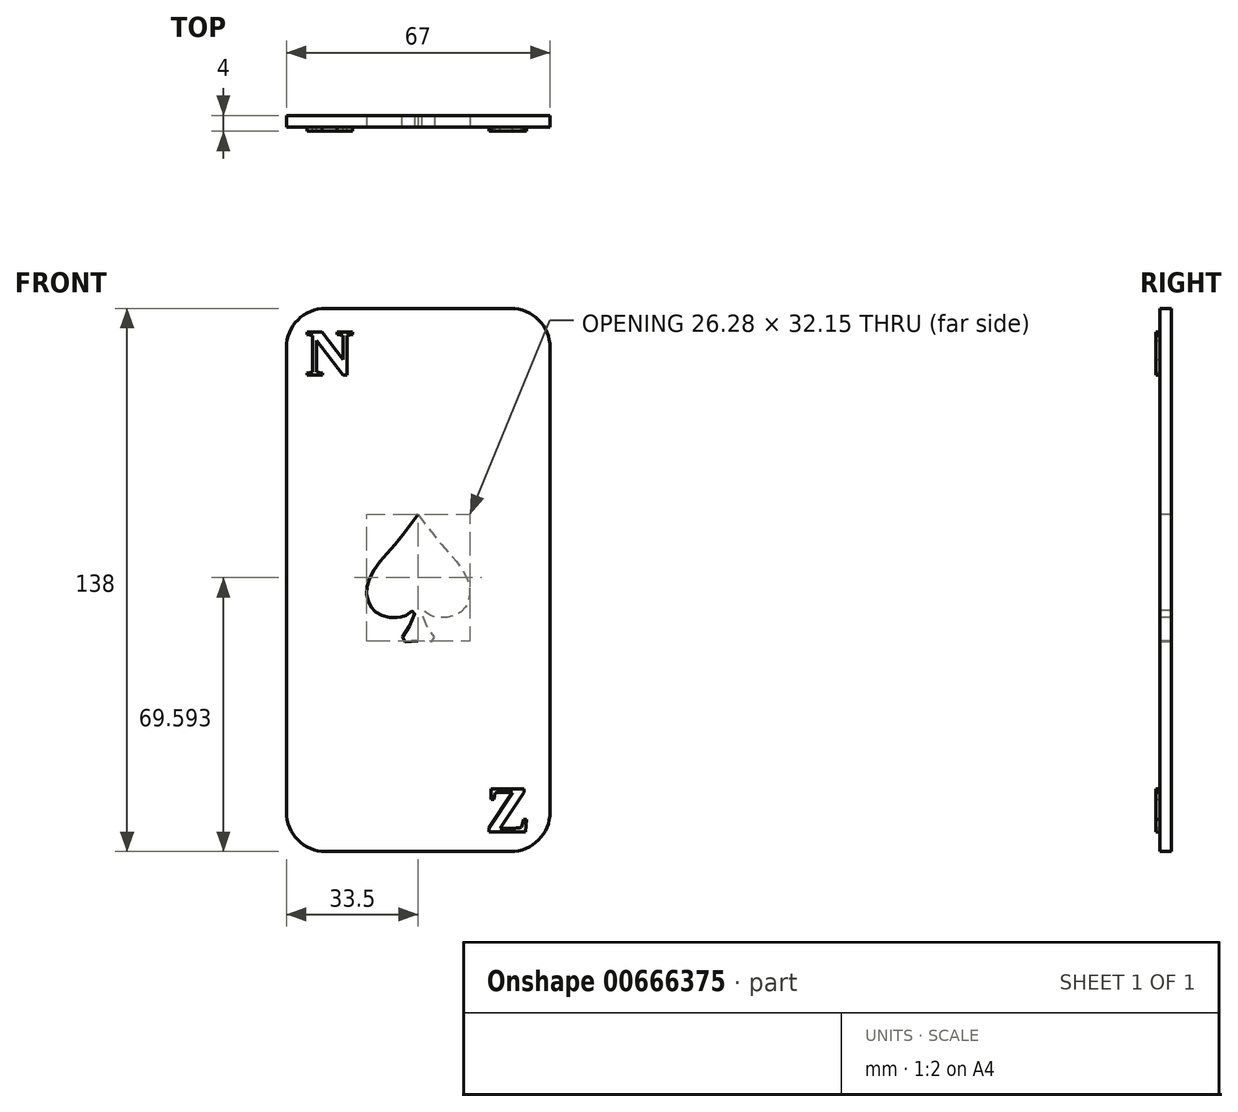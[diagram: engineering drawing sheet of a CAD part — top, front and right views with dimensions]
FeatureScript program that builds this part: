
annotation { "Feature Type Name" : "Feature", "Feature Type Description" : "" }
export const myFeature = defineFeature(function(context is Context, id is Id, definition is map)
    precondition{}
    {
        {
            var Q0;
            Q0=qCreatedBy(makeId("Front.planeOp"),FACE);
            var sketch = newSketch(context, id + "F0", { "sketchPlane" : qUnion([Q0])});
            skLineSegment(sketch, "E0.bottom", {"start": v(-23.5, 69) * mm, "end": v(23.5, 69) * mm});
            skLineSegment(sketch, "E0.top", {"start": v(-23.5, -69) * mm, "end": v(23.5, -69) * mm});
            skLineSegment(sketch, "E0.left", {"start": v(-33.5, 59) * mm, "end": v(-33.5, -59) * mm});
            skLineSegment(sketch, "E0.right", {"start": v(33.5, 59) * mm, "end": v(33.5, -59) * mm});
            skPoint(sketch, "E1.visualSharp", {"position": v(-33.5, 69) * mm});
            skArc(sketch, "E1.filletArc", {"start": v(-23.5, 69) * mm, "mid": v(-30.57, 66.07) * mm, "end": v(-33.5, 59) * mm});
            skPoint(sketch, "E2.visualSharp", {"position": v(33.5, 69) * mm});
            skArc(sketch, "E2.filletArc", {"start": v(33.5, 59) * mm, "mid": v(30.57, 66.07) * mm, "end": v(23.5, 69) * mm});
            skPoint(sketch, "E3.visualSharp", {"position": v(33.5, -69) * mm});
            skArc(sketch, "E3.filletArc", {"start": v(23.5, -69) * mm, "mid": v(30.57, -66.07) * mm, "end": v(33.5, -59) * mm});
            skPoint(sketch, "E4.visualSharp", {"position": v(-33.5, -69) * mm});
            skArc(sketch, "E4.filletArc", {"start": v(-33.5, -59) * mm, "mid": v(-30.57, -66.07) * mm, "end": v(-23.5, -69) * mm});
            skSolve(sketch);
        }
        {
            var Q0;
            Q0=makeQuery(id+"F0.imprint","IMPRINT",FACE,{"disambiguationData":[TD([[makeQuery(id+"F0.imprint","IMPRINT",EDGE,{"derivedFrom":sQuery(id+"F0.wireOp",EDGE,"E0.bottom")}),-1.0]])]});
            var sketch = newSketch(context, id + "F1", { "sketchPlane" : qUnion([Q0])});
            skText(sketch, "E5", { "text": "N", "fontName": "Tinos-Bold.ttf"});
            skText(sketch, "E6", { "text": "Z", "fontName": "Tinos-Bold.ttf"});
            const initialGuessF1  = {"E5": [-0.0285, 0.052, 1, 0, 0.012], "E6": [0.01719, -0.064, 1, 0, 0.012]};
            skSetInitialGuess(sketch, initialGuessF1);
            skSolve(sketch);
        }
        {
            var Q0;
            Q0=makeQuery(id+"F0.imprint","IMPRINT",FACE,{"disambiguationData":[TD([[makeQuery(id+"F0.imprint","IMPRINT",EDGE,{"derivedFrom":sQuery(id+"F0.wireOp",EDGE,"E0.bottom")}),-1.0]])]});
            var sketch = newSketch(context, id + "F2", { "sketchPlane" : qUnion([Q0])});
            skFitSpline(sketch, "E7", {"points": [v(0, 16.67) * mm, v(-3.59, 11.84) * mm, v(-7.27, 7.34) * mm, v(-10.17, 4.1) * mm, v(-12.13, 1) * mm, v(-13.02, -1.58) * mm, v(-13.06, -3.97) * mm, v(-12.55, -5.85) * mm, v(-11.95, -7.02) * mm, v(-10.8, -8.14) * mm, v(-8.93, -9.16) * mm, v(-6.8, -9.59) * mm, v(-5.13, -9.52) * mm, v(-4.55, -9.44) * mm, v(-3.77, -9.31) * mm, v(-2.5, -8.72) * mm, v(-1.05, -7.78) * mm, v(-1.64, -10.82) * mm, v(-4.15, -15.36) * mm, v(0, -15.48) * mm], "startDerivative": vector(-43.7, -59.68) * mm, "endDerivative": vector(87, 12.12) * mm});
            skFitSpline(sketch, "E8.MirrorCS", {"points": [v(0, 16.67) * mm, v(3.59, 11.84) * mm, v(7.27, 7.34) * mm, v(10.17, 4.1) * mm, v(12.13, 1) * mm, v(13.02, -1.58) * mm, v(13.06, -3.97) * mm, v(12.55, -5.85) * mm, v(11.95, -7.02) * mm, v(10.8, -8.14) * mm, v(8.93, -9.16) * mm, v(6.8, -9.59) * mm, v(5.13, -9.52) * mm, v(4.55, -9.44) * mm, v(3.77, -9.31) * mm, v(2.5, -8.72) * mm, v(1.05, -7.78) * mm, v(1.64, -10.82) * mm, v(4.15, -15.36) * mm, v(0, -15.48) * mm], "startDerivative": vector(43.7, -59.68) * mm, "endDerivative": vector(-87, 12.12) * mm});
            skSolve(sketch);
        }
        {
            var Q0;
            Q0=makeQuery(id+"F0.imprint","IMPRINT",FACE,{"disambiguationData":[TD([[makeQuery(id+"F0.imprint","IMPRINT",EDGE,{"derivedFrom":sQuery(id+"F0.wireOp",EDGE,"E0.bottom")}),-1.0]])]});
            extrude(context, id + "F3", {"entities" : qUnion([Q0]), "depth" : 3 * mm, "offsetDistance" : 25 * mm});
        }
        {
            var Q0;
            Q0=makeQuery(id+"F2.imprint","IMPRINT",FACE,{"disambiguationData":[TD([[makeQuery(id+"F2.imprint","IMPRINT",EDGE,{"derivedFrom":sQuery(id+"F2.wireOp",EDGE,"E7")}),1.0]])]});
            extrude(context, id + "F4", {"entities" : qUnion([Q0]), "operationType" : NewBodyOperationType.REMOVE, "endBound" : BoundingType.SYMMETRIC, "oppositeDirection" : true, "depth" : 25 * mm, "offsetDistance" : 25 * mm});
        }
        {
            var Q0;
            Q0 = qSketchRegion(id + "F1", true);
            extrude(context, id + "F5", {"entities" : qUnion([Q0]), "operationType" : NewBodyOperationType.ADD, "depth" : 4 * mm, "offsetDistance" : 25 * mm});
        }
    });
